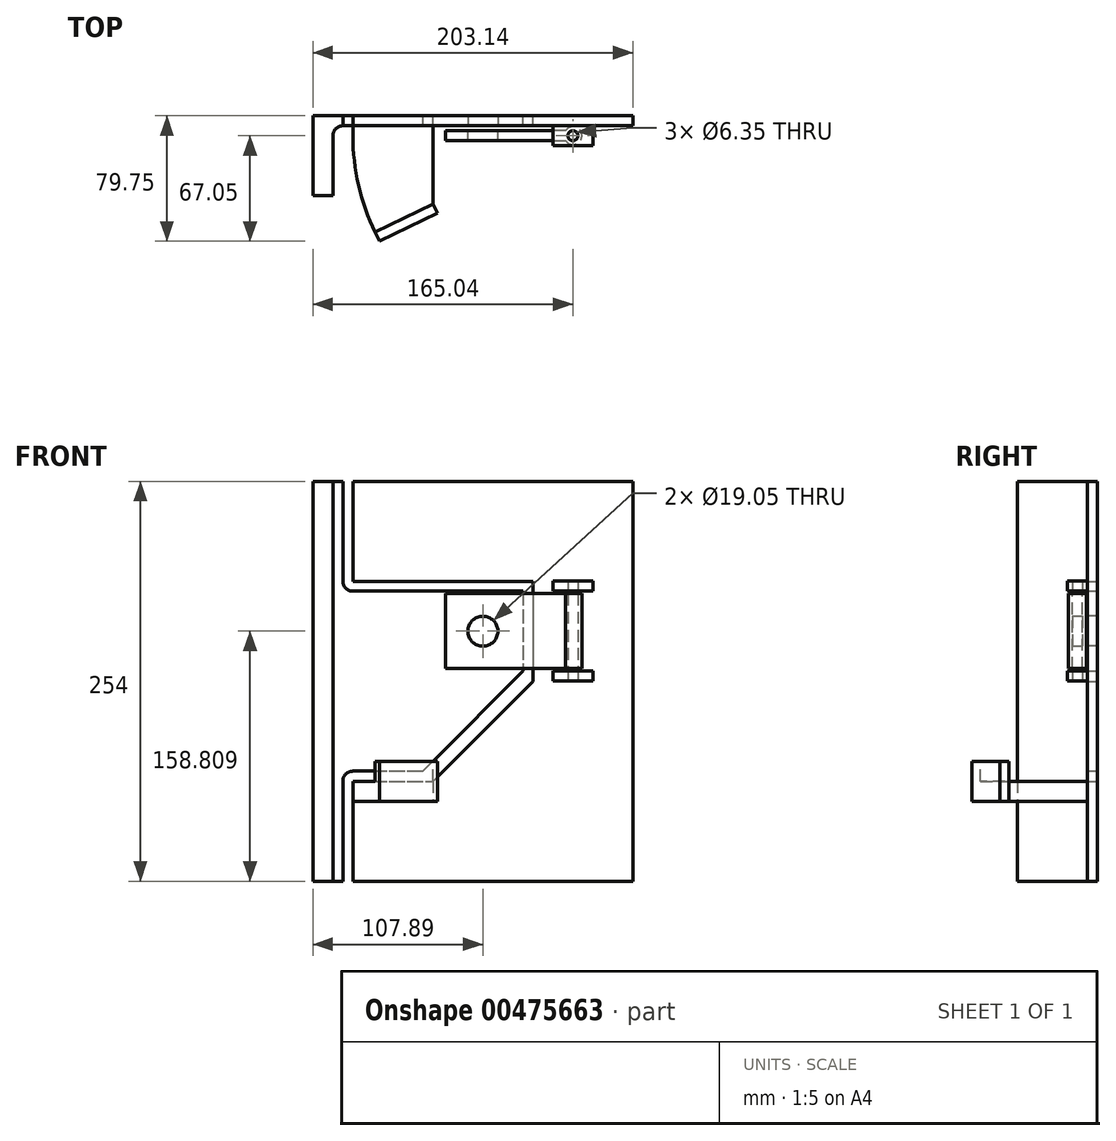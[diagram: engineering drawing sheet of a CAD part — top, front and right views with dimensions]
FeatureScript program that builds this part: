
annotation { "Feature Type Name" : "Feature", "Feature Type Description" : "" }
export const myFeature = defineFeature(function(context is Context, id is Id, definition is map)
    precondition{}
    {
        {
            var Q0;
            Q0=qCreatedBy(makeId("Front.planeOp"),FACE);
            var sketch = newSketch(context, id + "F0", { "sketchPlane" : qUnion([Q0])});
            skLineSegment(sketch, "E0", {"start": v(0, 0) * mm, "end": v(177.8, 0) * mm});
            skLineSegment(sketch, "E1", {"start": v(177.8, 0) * mm, "end": v(177.8, -254) * mm});
            skLineSegment(sketch, "E2", {"start": v(177.8, -254) * mm, "end": v(0, -254) * mm});
            skLineSegment(sketch, "E3", {"start": v(0, -254) * mm, "end": v(0, -190.5) * mm});
            skLineSegment(sketch, "E4", {"start": v(114.3, -63.5) * mm, "end": v(0, -63.5) * mm});
            skLineSegment(sketch, "E5", {"start": v(0, -63.5) * mm, "end": v(0, 0) * mm});
            skLineSegment(sketch, "E6", {"start": v(0, -190.5) * mm, "end": v(50.8, -190.5) * mm});
            skLineSegment(sketch, "E7", {"start": v(114.3, -63.5) * mm, "end": v(114.3, -127) * mm});
            skLineSegment(sketch, "E8", {"start": v(50.8, -190.5) * mm, "end": v(114.3, -127) * mm});
            skSolve(sketch);
        }
        {
            var Q0;
            Q0=makeQuery(id+"F0.imprint","IMPRINT",FACE,{"disambiguationData":[TD([[makeQuery(id+"F0.imprint","IMPRINT",EDGE,{"derivedFrom":sQuery(id+"F0.wireOp",EDGE,"E0")}),-1.0]])]});
            extrude(context, id + "F1", {"entities" : qUnion([Q0]), "depth" : 6.35 * mm});
        }
        {
            var Q0;
            Q0=qCreatedBy(makeId("Front.planeOp"),FACE);
            var sketch = newSketch(context, id + "F2", { "sketchPlane" : qUnion([Q0])});
            skPoint(sketch, "E9.0", {"position": v(0, -63.5) * mm});
            skLineSegment(sketch, "E10", {"start": v(0, -69.8) * mm, "end": v(107.95, -69.8) * mm});
            skLineSegment(sketch, "E11", {"start": v(107.95, -69.8) * mm, "end": v(107.95, -120.6) * mm});
            skLineSegment(sketch, "E12", {"start": v(0, -184.1) * mm, "end": v(44.45, -184.1) * mm});
            skLineSegment(sketch, "E13", {"start": v(44.45, -184.1) * mm, "end": v(107.95, -120.6) * mm});
            skArc(sketch, "E14", {"start": v(0, -69.8) * mm, "mid": v(-4.45, -67.95) * mm, "end": v(-6.3, -63.5) * mm});
            skLineSegment(sketch, "E15", {"start": v(-6.3, -63.5) * mm, "end": v(-6.3, 0) * mm});
            skLineSegment(sketch, "E16", {"start": v(-6.3, 0) * mm, "end": v(-25.34, 0) * mm});
            skLineSegment(sketch, "E17", {"start": v(-25.34, 0) * mm, "end": v(-25.34, -254) * mm});
            skLineSegment(sketch, "E18", {"start": v(-25.34, -254) * mm, "end": v(-6.3, -254) * mm});
            skPoint(sketch, "E19.0", {"position": v(0, -190.5) * mm});
            skArc(sketch, "E20", {"start": v(0, -184.1) * mm, "mid": v(-4.53, -185.97) * mm, "end": v(-6.4, -190.5) * mm});
            skLineSegment(sketch, "E21", {"start": v(-6.3, -254) * mm, "end": v(-6.4, -190.5) * mm});
            skSolve(sketch);
        }
        {
            var Q0;
            Q0=makeQuery(id+"F2.imprint","IMPRINT",FACE,{"disambiguationData":[TD([[makeQuery(id+"F2.imprint","IMPRINT",EDGE,{"derivedFrom":sQuery(id+"F2.wireOp",EDGE,"E10")}),-1.0]])]});
            extrude(context, id + "F3", {"entities" : qUnion([Q0]), "depth" : 6.35 * mm});
        }
        {
            var Q0;
            Q0=makeQuery(id+"F3.opExtrude","CAP_FACE",FACE,{"disambiguationData":[OSD([sQuery(id+"F2.wireOp",EDGE,"E10"),sQuery(id+"F2.wireOp",EDGE,"E11"),sQuery(id+"F2.wireOp",EDGE,"E12"),sQuery(id+"F2.wireOp",EDGE,"E13"),sQuery(id+"F2.wireOp",EDGE,"E14"),sQuery(id+"F2.wireOp",EDGE,"E15"),sQuery(id+"F2.wireOp",EDGE,"E16"),sQuery(id+"F2.wireOp",EDGE,"E17"),sQuery(id+"F2.wireOp",EDGE,"E18"),sQuery(id+"F2.wireOp",EDGE,"E20"),sQuery(id+"F2.wireOp",EDGE,"E21")])],"isStart":false});
            var sketch = newSketch(context, id + "F4", { "sketchPlane" : qUnion([Q0])});
            skLineSegment(sketch, "E22", {"start": v(107.95, -69.8) * mm, "end": v(82.55, -69.8) * mm, "construction": true});
            skLineSegment(sketch, "E23", {"start": v(82.55, -69.8) * mm, "end": v(82.55, -95.2) * mm, "construction": true});
            skCircle(sketch, "E24", {"center": v(82.55, -95.2) * mm, "radius": 9.53 * mm});
            skSolve(sketch);
        }
        {
            var Q0;
            Q0=makeQuery(id+"F4.imprint","IMPRINT",FACE,{"disambiguationData":[TD([[makeQuery(id+"F4.imprint","IMPRINT",EDGE,{"derivedFrom":sQuery(id+"F4.wireOp",EDGE,"E24")}),1.0]])]});
            extrude(context, id + "F5", {"entities" : qUnion([Q0]), "operationType" : NewBodyOperationType.REMOVE, "endBound" : BoundingType.UP_TO_NEXT, "oppositeDirection" : true, "depth" : 25.4 * mm});
        }
        {
            var Q0;
            Q0=makeQuery(id+"F1.opExtrude","CAP_FACE",FACE,{"disambiguationData":[OSD([sQuery(id+"F0.wireOp",EDGE,"E0"),sQuery(id+"F0.wireOp",EDGE,"E1"),sQuery(id+"F0.wireOp",EDGE,"E2"),sQuery(id+"F0.wireOp",EDGE,"E3"),sQuery(id+"F0.wireOp",EDGE,"E4"),sQuery(id+"F0.wireOp",EDGE,"E5"),sQuery(id+"F0.wireOp",EDGE,"E6"),sQuery(id+"F0.wireOp",EDGE,"E7"),sQuery(id+"F0.wireOp",EDGE,"E8")])],"isStart":false});
            var sketch = newSketch(context, id + "F6", { "sketchPlane" : qUnion([Q0])});
            skCircle(sketch, "E25.0", {"center": v(82.55, -95.2) * mm, "radius": 9.53 * mm, "construction": true});
            skLineSegment(sketch, "E26", {"start": v(82.55, -95.2) * mm, "end": v(139.7, -95.2) * mm, "construction": true});
            skLineSegment(sketch, "E27", {"start": v(139.7, -95.2) * mm, "end": v(139.7, -69.8) * mm, "construction": true});
            skLineSegment(sketch, "E28", {"start": v(139.7, -69.8) * mm, "end": v(127, -69.8) * mm, "construction": true});
            skLineSegment(sketch, "E29", {"start": v(127, -69.8) * mm, "end": v(152.4, -69.8) * mm});
            skLineSegment(sketch, "E30", {"start": v(127, -69.8) * mm, "end": v(127, -63.44) * mm});
            skLineSegment(sketch, "E31", {"start": v(127, -63.44) * mm, "end": v(152.4, -63.44) * mm});
            skLineSegment(sketch, "E32", {"start": v(152.4, -63.44) * mm, "end": v(152.4, -69.8) * mm});
            skLineSegment(sketch, "E33", {"start": v(139.7, -120.6) * mm, "end": v(127, -120.6) * mm});
            skLineSegment(sketch, "E34", {"start": v(127, -120.6) * mm, "end": v(127, -126.94) * mm});
            skLineSegment(sketch, "E35", {"start": v(127, -126.94) * mm, "end": v(152.4, -126.94) * mm});
            skLineSegment(sketch, "E36", {"start": v(152.4, -126.94) * mm, "end": v(152.4, -120.6) * mm});
            skLineSegment(sketch, "E37", {"start": v(152.4, -120.6) * mm, "end": v(139.7, -120.6) * mm});
            skLineSegment(sketch, "E38", {"start": v(139.7, -95.2) * mm, "end": v(139.7, -120.6) * mm, "construction": true});
            skSolve(sketch);
        }
        {
            var Q0;
            Q0=makeQuery(id+"F6.imprint","IMPRINT",FACE,{"disambiguationData":[TD([[makeQuery(id+"F6.imprint","IMPRINT",EDGE,{"derivedFrom":sQuery(id+"F6.wireOp",EDGE,"E29")}),1.0]])]});
            var Q1;
            Q1=makeQuery(id+"F6.imprint","IMPRINT",FACE,{"disambiguationData":[TD([[makeQuery(id+"F6.imprint","IMPRINT",EDGE,{"derivedFrom":sQuery(id+"F6.wireOp",EDGE,"E33")}),1.0]])]});
            extrude(context, id + "F7", {"entities" : qUnion([Q0, Q1]), "operationType" : NewBodyOperationType.ADD, "depth" : 12.7 * mm});
        }
        {
            var Q0;
            Q0=makeQuery(id+"F7.opExtrude","SWEPT_FACE",FACE,{"disambiguationData":[OSD([sQuery(id+"F6.wireOp",EDGE,"E35")])]});
            var sketch = newSketch(context, id + "F8", { "sketchPlane" : qUnion([Q0])});
            skPoint(sketch, "E39.endSnap0", {"position": v(139.7, 19.05) * mm});
            skCircle(sketch, "E40", {"center": v(139.7, 12.7) * mm, "radius": 3.18 * mm});
            skSolve(sketch);
        }
        {
            var Q0;
            Q0=makeQuery(id+"F8.imprint","IMPRINT",FACE,{"disambiguationData":[TD([[makeQuery(id+"F8.imprint","IMPRINT",EDGE,{"derivedFrom":sQuery(id+"F8.wireOp",EDGE,"E40")}),1.0]])]});
            var Q1;
            Q1=makeQuery(id+"F7.opExtrude","SWEPT_FACE",FACE,{"disambiguationData":[OSD([sQuery(id+"F6.wireOp",EDGE,"E31")])]});
            extrude(context, id + "F9", {"entities" : qUnion([Q0]), "operationType" : NewBodyOperationType.REMOVE, "endBound" : BoundingType.UP_TO_SURFACE, "oppositeDirection" : true, "endBoundEntityFace" : qUnion([Q1]), "depth" : 25.4 * mm, "hasSecondDirection" : true, "secondDirectionOppositeDirection" : false, "secondDirectionDepth" : 25.4 * mm});
        }
        {
            var Q0;
            Q0=makeQuery(id+"F7.opExtrude","SWEPT_FACE",FACE,{"disambiguationData":[OSD([sQuery(id+"F6.wireOp",EDGE,"E29")])]});
            var sketch = newSketch(context, id + "F10", { "sketchPlane" : qUnion([Q0])});
            skLineSegment(sketch, "E41", {"start": v(139.7, 12.7) * mm, "end": v(139.7, 15.88) * mm, "construction": true});
            skLineSegment(sketch, "E42", {"start": v(139.7, 15.88) * mm, "end": v(134.95, 15.88) * mm, "construction": true});
            skLineSegment(sketch, "E43", {"start": v(134.95, 15.88) * mm, "end": v(134.95, 9.53) * mm, "construction": true});
            skLineSegment(sketch, "E44", {"start": v(134.95, 15.88) * mm, "end": v(58.75, 15.88) * mm});
            skLineSegment(sketch, "E45", {"start": v(58.75, 15.87) * mm, "end": v(58.75, 9.52) * mm});
            skLineSegment(sketch, "E46", {"start": v(58.75, 9.52) * mm, "end": v(134.95, 9.53) * mm});
            skCircle(sketch, "E47", {"center": v(139.7, 12.7) * mm, "radius": 3.17 * mm});
            skCircle(sketch, "E48", {"center": v(139.7, 12.7) * mm, "radius": 5.72 * mm});
            skSolve(sketch);
        }
        {
            var Q0;
            {var subQ0=sQuery(id+"F10.wireOp",EDGE,"E48");var subQ1=sQuery(id+"F10.wireOp",EDGE,"E44");var subQ2=makeQuery(id+"F10.imprint","INTERSECT",VERTEX,{"derivedFrom":[subQ1,subQ0]});Q0=makeQuery(id+"F10.imprint","IMPRINT",FACE,{"disambiguationData":[TD([[makeQuery(id+"F10.imprint","IMPRINT",EDGE,{"disambiguationData":[TD([[subQ2,-1.0]])],"derivedFrom":subQ0}),-1.0]])]});}
            var Q1;
            Q1=makeQuery(id+"F10.imprint","IMPRINT",FACE,{"disambiguationData":[TD([[makeQuery(id+"F10.imprint","IMPRINT",EDGE,{"derivedFrom":sQuery(id+"F10.wireOp",EDGE,"E47")}),1.0]])]});
            var Q2;
            {var subQ0=sQuery(id+"F10.wireOp",EDGE,"E45");Q2=makeQuery(id+"F10.imprint","IMPRINT",FACE,{"disambiguationData":[TD([[makeQuery(id+"F10.imprint","IMPRINT",EDGE,{"derivedFrom":subQ0}),1.0]])]});}
            var Q3;
            Q3=makeQuery(id+"F7.opExtrude","SWEPT_FACE",FACE,{"disambiguationData":[OSD([sQuery(id+"F6.wireOp",EDGE,"E33"),sQuery(id+"F6.wireOp",EDGE,"E37")])]});
            extrude(context, id + "F11", {"entities" : qUnion([Q0, Q1, Q2]), "operationType" : NewBodyOperationType.ADD, "endBound" : BoundingType.UP_TO_SURFACE, "endBoundEntityFace" : qUnion([Q3]), "depth" : 25.4 * mm});
        }
        {
            var Q0;
            Q0=makeQuery(id+"F11.opExtrude","SWEPT_FACE",FACE,{"disambiguationData":[OSD([sQuery(id+"F10.wireOp",EDGE,"E46")])]});
            var sketch = newSketch(context, id + "F12", { "sketchPlane" : qUnion([Q0])});
            skCircle(sketch, "E49.0", {"center": v(-82.55, -95.2) * mm, "radius": 9.53 * mm});
            skSolve(sketch);
        }
        {
            var Q0;
            Q0=makeQuery(id+"F12.imprint","IMPRINT",FACE,{"disambiguationData":[TD([[makeQuery(id+"F12.imprint","IMPRINT",EDGE,{"derivedFrom":sQuery(id+"F12.wireOp",EDGE,"E49.0")}),1.0]])]});
            extrude(context, id + "F13", {"entities" : qUnion([Q0]), "operationType" : NewBodyOperationType.REMOVE, "endBound" : BoundingType.UP_TO_NEXT, "oppositeDirection" : true, "depth" : 25.4 * mm});
        }
        {
            var Q0;
            Q0=makeQuery(id+"F11.opExtrude","SWEPT_FACE",FACE,{"disambiguationData":[OSD([sQuery(id+"F10.wireOp",EDGE,"E45")])]});
            var sketch = newSketch(context, id + "F14", { "sketchPlane" : qUnion([Q0])});
            skPoint(sketch, "E50.0", {"position": v(19.05, -69.8) * mm});
            skPoint(sketch, "E51.0", {"position": v(6.35, -69.8) * mm});
            skLineSegment(sketch, "E52", {"start": v(19.05, -69.8) * mm, "end": v(6.35, -69.8) * mm});
            skLineSegment(sketch, "E53", {"start": v(19.05, -69.8) * mm, "end": v(19.05, -71.38) * mm});
            skLineSegment(sketch, "E54", {"start": v(19.05, -71.38) * mm, "end": v(6.35, -71.38) * mm});
            skLineSegment(sketch, "E55", {"start": v(6.35, -71.38) * mm, "end": v(6.35, -69.8) * mm});
            skPoint(sketch, "E56.0", {"position": v(19.05, -120.6) * mm});
            skPoint(sketch, "E57.0", {"position": v(6.35, -120.6) * mm});
            skLineSegment(sketch, "E58", {"start": v(6.35, -120.6) * mm, "end": v(6.35, -119) * mm});
            skLineSegment(sketch, "E59", {"start": v(6.35, -120.6) * mm, "end": v(19.05, -120.6) * mm});
            skLineSegment(sketch, "E60", {"start": v(19.05, -119) * mm, "end": v(6.35, -119) * mm});
            skLineSegment(sketch, "E61", {"start": v(19.05, -120.6) * mm, "end": v(19.05, -119) * mm});
            skSolve(sketch);
        }
        {
            var Q0;
            {var subQ3=sQuery(id+"F14.wireOp",EDGE,"E61");Q0=makeQuery(id+"F14.imprint","IMPRINT",FACE,{"disambiguationData":[TD([[makeQuery(id+"F14.imprint","IMPRINT",EDGE,{"derivedFrom":subQ3}),1.0]])]});}
            var Q1;
            {var subQ0=sQuery(id+"F14.wireOp",EDGE,"E59");var subQ1=sQuery(id+"F10.wireOp",EDGE,"E45");var subQ2=makeQuery(id+"F11.opExtrude","SWEPT_EDGE",EDGE,{"disambiguationData":[OSD([sQuery(id+"F10.wireOp",EDGE,"E44"),subQ1])]});var subQ3=makeQuery(id+"F14.imprint","INTERSECT",VERTEX,{"derivedFrom":[subQ2,subQ0]});var subQ4=makeQuery(id+"F11.opExtrude","SWEPT_EDGE",EDGE,{"disambiguationData":[OSD([subQ1,sQuery(id+"F10.wireOp",EDGE,"E46")])]});var subQ5=makeQuery(id+"F14.imprint","INTERSECT",VERTEX,{"derivedFrom":[subQ4,subQ0]});Q1=makeQuery(id+"F14.imprint","IMPRINT",FACE,{"disambiguationData":[TD([[makeQuery(id+"F14.imprint","IMPRINT",EDGE,{"disambiguationData":[TD([[subQ3,-1.0],[subQ5,1.0]])],"derivedFrom":subQ0}),-1.0]])]});}
            var Q2;
            {var subQ0=sQuery(id+"F14.wireOp",EDGE,"E58");Q2=makeQuery(id+"F14.imprint","IMPRINT",FACE,{"disambiguationData":[TD([[makeQuery(id+"F14.imprint","IMPRINT",EDGE,{"derivedFrom":subQ0}),-1.0]])]});}
            var Q3;
            {var subQ3=sQuery(id+"F14.wireOp",EDGE,"E55");Q3=makeQuery(id+"F14.imprint","IMPRINT",FACE,{"disambiguationData":[TD([[makeQuery(id+"F14.imprint","IMPRINT",EDGE,{"derivedFrom":subQ3}),-1.0]])]});}
            var Q4;
            {var subQ0=sQuery(id+"F14.wireOp",EDGE,"E52");var subQ1=sQuery(id+"F10.wireOp",EDGE,"E45");var subQ2=makeQuery(id+"F11.opExtrude","SWEPT_EDGE",EDGE,{"disambiguationData":[OSD([sQuery(id+"F10.wireOp",EDGE,"E44"),subQ1])]});var subQ3=makeQuery(id+"F14.imprint","INTERSECT",VERTEX,{"derivedFrom":[subQ2,subQ0]});Q4=makeQuery(id+"F14.imprint","IMPRINT",FACE,{"disambiguationData":[TD([[makeQuery(id+"F14.imprint","IMPRINT",EDGE,{"disambiguationData":[TD([[subQ3,-1.0]])],"derivedFrom":subQ0}),1.0]])]});}
            var Q5;
            {var subQ3=sQuery(id+"F14.wireOp",EDGE,"E53");Q5=makeQuery(id+"F14.imprint","IMPRINT",FACE,{"disambiguationData":[TD([[makeQuery(id+"F14.imprint","IMPRINT",EDGE,{"derivedFrom":subQ3}),-1.0]])]});}
            extrude(context, id + "F15", {"entities" : qUnion([Q0, Q1, Q2, Q3, Q4, Q5]), "operationType" : NewBodyOperationType.REMOVE, "endBound" : BoundingType.THROUGH_ALL, "oppositeDirection" : true, "depth" : 95 * mm});
        }
        {
            var Q0;
            Q0=makeQuery(id+"F3.opExtrude","SWEPT_FACE",FACE,{"disambiguationData":[OSD([sQuery(id+"F2.wireOp",EDGE,"E18")])]});
            var sketch = newSketch(context, id + "F16", { "sketchPlane" : qUnion([Q0])});
            skLineSegment(sketch, "E62", {"start": v(-25.34, 6.35) * mm, "end": v(-6.3, 6.35) * mm});
            skLineSegment(sketch, "E63", {"start": v(-25.34, 6.35) * mm, "end": v(-25.34, 50.8) * mm});
            skLineSegment(sketch, "E64", {"start": v(-25.34, 50.8) * mm, "end": v(-12.64, 50.8) * mm});
            skLineSegment(sketch, "E65", {"start": v(-12.64, 50.8) * mm, "end": v(-12.64, 12.7) * mm});
            skArc(sketch, "E66", {"start": v(-12.64, 12.7) * mm, "mid": v(-10.78, 8.2) * mm, "end": v(-6.3, 6.35) * mm});
            skSolve(sketch);
        }
        {
            var Q0;
            Q0=makeQuery(id+"F16.imprint","IMPRINT",FACE,{"disambiguationData":[TD([[makeQuery(id+"F16.imprint","IMPRINT",EDGE,{"derivedFrom":sQuery(id+"F16.wireOp",EDGE,"E62")}),1.0]])]});
            extrude(context, id + "F17", {"entities" : qUnion([Q0]), "operationType" : NewBodyOperationType.ADD, "oppositeDirection" : true, "depth" : 254 * mm});
        }
        {
            var Q0;
            Q0=makeQuery(id+"F1.opExtrude","CAP_FACE",FACE,{"disambiguationData":[OSD([sQuery(id+"F0.wireOp",EDGE,"E0"),sQuery(id+"F0.wireOp",EDGE,"E1"),sQuery(id+"F0.wireOp",EDGE,"E2"),sQuery(id+"F0.wireOp",EDGE,"E3"),sQuery(id+"F0.wireOp",EDGE,"E4"),sQuery(id+"F0.wireOp",EDGE,"E5"),sQuery(id+"F0.wireOp",EDGE,"E6"),sQuery(id+"F0.wireOp",EDGE,"E7"),sQuery(id+"F0.wireOp",EDGE,"E8")])],"isStart":false});
            var sketch = newSketch(context, id + "F18", { "sketchPlane" : qUnion([Q0])});
            skLineSegment(sketch, "E67.bottom", {"start": v(0, -190.5) * mm, "end": v(50.8, -190.5) * mm});
            skLineSegment(sketch, "E67.top", {"start": v(0, -203.2) * mm, "end": v(50.8, -203.2) * mm});
            skLineSegment(sketch, "E67.left", {"start": v(0, -190.5) * mm, "end": v(0, -203.2) * mm});
            skLineSegment(sketch, "E67.right", {"start": v(50.8, -190.5) * mm, "end": v(50.8, -203.2) * mm});
            skSolve(sketch);
        }
        {
            var Q0;
            Q0=makeQuery(id+"F18.imprint","IMPRINT",FACE,{"disambiguationData":[TD([[makeQuery(id+"F18.imprint","IMPRINT",EDGE,{"derivedFrom":sQuery(id+"F18.wireOp",EDGE,"E67.bottom")}),-1.0]])]});
            extrude(context, id + "F19", {"entities" : qUnion([Q0]), "operationType" : NewBodyOperationType.ADD, "depth" : 69.85 * mm});
        }
        {
            var Q0;
            Q0=makeQuery(id+"F19.boolean.opBoolean","MERGE",FACE,{"derivedFrom":[makeQuery(id+"F1.opExtrude","SWEPT_FACE",FACE,{"disambiguationData":[OSD([sQuery(id+"F0.wireOp",EDGE,"E6")])]}),makeQuery(id+"F19.opExtrude","SWEPT_FACE",FACE,{"disambiguationData":[OSD([sQuery(id+"F18.wireOp",EDGE,"E67.bottom")])]})]});
            var sketch = newSketch(context, id + "F20", { "sketchPlane" : qUnion([Q0])});
            skLineSegment(sketch, "E68.0.0", {"start": v(152.4, -6.35) * mm, "end": v(127, -6.35) * mm});
            skLineSegment(sketch, "E68.0.1", {"start": v(127, -6.35) * mm, "end": v(127, -19.05) * mm});
            skLineSegment(sketch, "E68.0.2", {"start": v(127, -19.05) * mm, "end": v(152.4, -19.05) * mm});
            skLineSegment(sketch, "E68.0.3", {"start": v(152.4, -19.05) * mm, "end": v(152.4, -6.35) * mm});
            skCircle(sketch, "E69.0", {"center": v(139.7, -12.7) * mm, "radius": 3.18 * mm});
            skArc(sketch, "E70", {"start": v(0, -12.7) * mm, "mid": v(3.6, -44.18) * mm, "end": v(14.2, -74.05) * mm});
            skLineSegment(sketch, "E71", {"start": v(14.2, -74.05) * mm, "end": v(50.8, -56.15) * mm});
            skLineSegment(sketch, "E72", {"start": v(50.8, -56.15) * mm, "end": v(50.8, -76.2) * mm});
            skLineSegment(sketch, "E73", {"start": v(50.8, -76.2) * mm, "end": v(0, -76.2) * mm});
            skLineSegment(sketch, "E74", {"start": v(0, -76.2) * mm, "end": v(0, -12.7) * mm});
            skSolve(sketch);
        }
        {
            var Q0;
            Q0=makeQuery(id+"F20.imprint","IMPRINT",FACE,{"disambiguationData":[TD([[makeQuery(id+"F20.imprint","IMPRINT",EDGE,{"derivedFrom":sQuery(id+"F20.wireOp",EDGE,"E70")}),-1.0]])]});
            extrude(context, id + "F21", {"entities" : qUnion([Q0]), "operationType" : NewBodyOperationType.REMOVE, "endBound" : BoundingType.UP_TO_NEXT, "oppositeDirection" : true, "depth" : 25.4 * mm});
        }
        {
            var Q0;
            Q0=makeQuery(id+"F21.boolean.opBoolean","COPY",FACE,{"derivedFrom":makeQuery(id+"F21.opExtrude","SWEPT_FACE",FACE,{"disambiguationData":[OSD([sQuery(id+"F20.wireOp",EDGE,"E71")])]})});
            var sketch = newSketch(context, id + "F22", { "sketchPlane" : qUnion([Q0])});
            skLineSegment(sketch, "E75", {"start": v(-19.77, -203.2) * mm, "end": v(20.98, -203.2) * mm});
            skLineSegment(sketch, "E76", {"start": v(20.98, -203.2) * mm, "end": v(20.98, -177.8) * mm});
            skLineSegment(sketch, "E77", {"start": v(-19.77, -203.2) * mm, "end": v(-19.77, -177.8) * mm});
            skLineSegment(sketch, "E78", {"start": v(-19.77, -177.8) * mm, "end": v(20.98, -177.8) * mm});
            skSolve(sketch);
        }
        {
            var Q0;
            {var subQ2=sQuery(id+"F22.wireOp",EDGE,"E78");Q0=makeQuery(id+"F22.imprint","IMPRINT",FACE,{"disambiguationData":[TD([[makeQuery(id+"F22.imprint","IMPRINT",EDGE,{"derivedFrom":subQ2}),-1.0]])]});}
            var Q1;
            {var subQ0=sQuery(id+"F22.wireOp",EDGE,"E75");Q1=makeQuery(id+"F22.imprint","IMPRINT",FACE,{"disambiguationData":[TD([[makeQuery(id+"F22.imprint","IMPRINT",EDGE,{"derivedFrom":subQ0}),-1.0]])]});}
            extrude(context, id + "F23", {"entities" : qUnion([Q0, Q1]), "operationType" : NewBodyOperationType.ADD, "depth" : 6.35 * mm});
        }
    });
